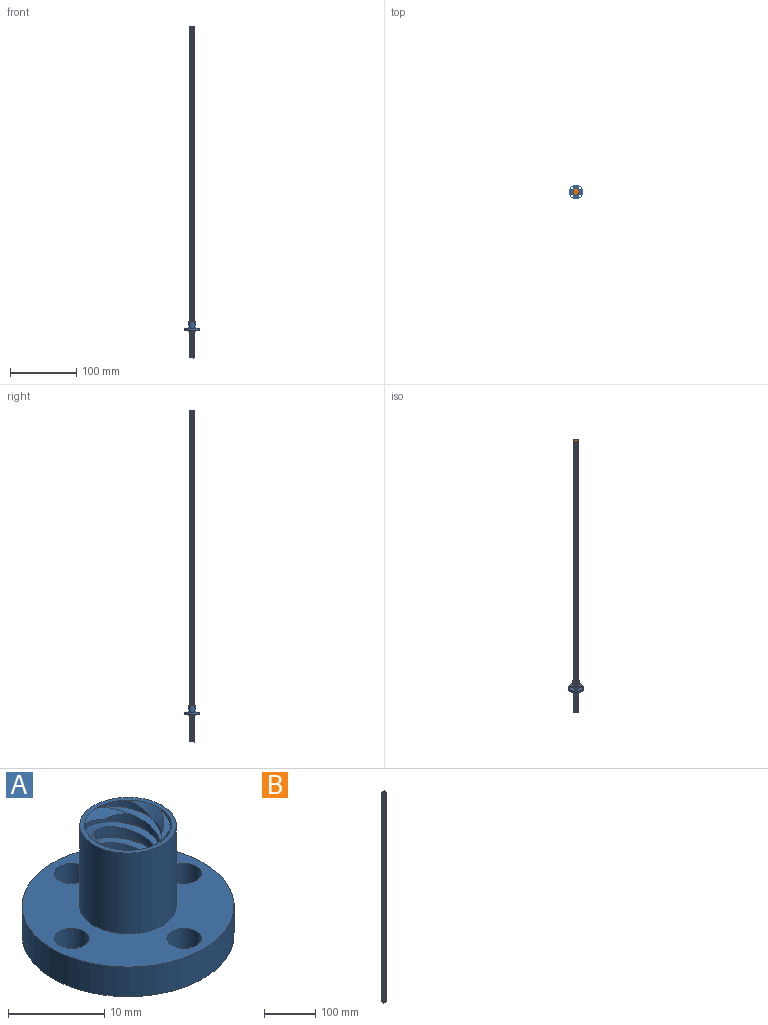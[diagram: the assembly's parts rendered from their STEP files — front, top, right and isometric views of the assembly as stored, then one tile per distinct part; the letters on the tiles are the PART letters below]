
ASSEMBLY  parts=2 mates=1
PART A: 29 faces, bbox 22x22x16 mm
  f0: cylinder r=3.5mm len=13.7mm, axis (0,0,-1), area 54.8mm2, adj f1,f26,f27,f28
  f1: cone r=4.5mm half-angle=45deg, axis (0,0,-1), area 17.8mm2, adj f0,f2,f3,f4,f5,f6,f17,f18
  f2: cylinder r=4.5mm len=15.7mm, axis (0,0,1), area 55.5mm2, adj f1,f3,f26,f27
  f3: bspline ~16x9mm, area 48.6mm2, adj f1,f2,f4,f27
  f4: cylinder r=3.5mm len=13.7mm, axis (0,0,-1), area 54.9mm2, adj f1,f3,f5,f27
  f5: bspline ~16x9mm, area 48.6mm2, adj f1,f4,f17,f27
  f6: plane 10.03x10.03mm, normal (0,0,-1), area 15.4mm2, adj f1,f7
  f7: cylinder r=5.02mm len=10.03mm, axis (0,0,1), area 53.6mm2, adj f6,f8
  f8: plane 22x22mm, normal (0,0,-1), area 260.4mm2, adj f7,f9,f13,f14,f15,f16
  f9: cylinder r=11mm len=22mm, axis (0,0,-1), area 259.2mm2, adj f8,f10
  f10: plane 22x22mm, normal (0,0,1), area 260.4mm2, adj f9,f11,f13,f14,f15,f16
  f11: cylinder r=5.02mm len=10.25mm, axis (0,0,-1), area 323mm2, adj f10,f12
  f12: plane 10.03x10.03mm, normal (0,0,1), area 15.4mm2, adj f11,f27
  f13: cylinder r=1.8mm len=3.75mm, axis (0,0,-1), area 42.4mm2, adj f8,f10
  f14: cylinder r=1.8mm len=3.75mm, axis (0,0,-1), area 42.4mm2, adj f8,f10
  f15: cylinder r=1.8mm len=3.75mm, axis (0,0,-1), area 42.4mm2, adj f8,f10
  f16: cylinder r=1.8mm len=3.75mm, axis (0,0,-1), area 42.4mm2, adj f8,f10
  f17: cylinder r=4.5mm len=15.7mm, axis (0,0,1), area 55.5mm2, adj f1,f5,f18,f27
  f18: bspline ~16x9mm, area 48.6mm2, adj f1,f17,f19,f27
  f19: cylinder r=3.5mm len=13.7mm, axis (0,0,-1), area 35.9mm2, adj f1,f18,f20,f27
  f20: bspline ~16x9mm, area 48.6mm2, adj f1,f19,f21,f27
  f21: cylinder r=4.5mm len=15.7mm, axis (0,0,1), area 55.5mm2, adj f1,f20,f22,f27
  f22: bspline ~16x9mm, area 48.6mm2, adj f1,f21,f23,f27
  f23: cylinder r=3.5mm len=13.7mm, axis (0,0,-1), area 48.1mm2, adj f1,f22,f24,f27
  f24: bspline ~16x9mm, area 48.6mm2, adj f1,f23,f25,f27
  f25: cylinder r=4.5mm len=15.7mm, axis (0,0,1), area 55.5mm2, adj f1,f24,f27,f28
  f26: bspline ~16x9mm, area 48.6mm2, adj f0,f1,f2,f27
  f27: cone r=3.5mm half-angle=45deg, axis (0,0,1), area 17.8mm2, adj f0,f2,f3,f4,f5,f12,f17,f18
  f28: bspline ~16x9mm, area 48.6mm2, adj f0,f1,f25,f27
PART B: 30 faces, bbox 8x8x501 mm
  f0: cylinder r=4mm len=499mm, axis (0,0,-1), area -3136.1mm2, adj f5,f7,f13,f25,f28
  f1: cylinder r=4mm len=499mm, axis (0,0,-1), area -3118.7mm2, adj f5,f6,f12,f14,f23
  f2: cylinder r=4mm len=499mm, axis (0,0,-1), area -3136.1mm2, adj f4,f11,f17,f20,f24
  f3: plane 7x7mm, normal (0,0,1), area 33.4mm2, adj f6,f7,f8,f11,f13,f14,f15,f17
  f4: cone r=4mm half-angle=45deg, axis (0,0,1), area 7.3mm2, adj f2,f9,f10,f16,f17,f20,f29
  f5: cone r=4mm half-angle=45deg, axis (0,0,1), area 7.3mm2, adj f0,f1,f9,f12,f13,f23,f25
  f6: cone r=3.5mm half-angle=45deg, axis (0,0,-1), area 2.1mm2, adj f1,f3,f14,f22,f23
  f7: cone r=3.5mm half-angle=45deg, axis (0,0,-1), area 2.1mm2, adj f0,f3,f13,f28
  f8: cone r=3.5mm half-angle=45deg, axis (0,0,-1), area 2.1mm2, adj f3,f10,f19,f27,f29
  f9: plane 7x7mm, normal (0,0,-1), area 38.5mm2, adj f4,f5,f20,f21,f23,f25,f26,f29
  f10: cylinder r=4mm len=499mm, axis (0,0,-1), area -3118.7mm2, adj f4,f8,f16,f19,f29
  f11: cone r=3.5mm half-angle=45deg, axis (0,0,-1), area 2.1mm2, adj f2,f3,f17,f24
  f12: plane 1x1mm, normal (-1,0,0), area 0.9mm2, adj f1,f5,f13,f14,f15
  f13: bspline ~500x8mm, area 1456.8mm2, adj f0,f3,f5,f7,f12,f15
  f14: bspline ~499x8mm, area 1463.5mm2, adj f1,f3,f6,f12,f15
  f15: cylinder r=3mm len=499.99mm, axis (0,0,-1), area 2179.1mm2, adj f3,f12,f13,f14
  f16: plane 1x1mm, normal (1,0,0), area 0.9mm2, adj f4,f10,f17,f18,f19
  f17: bspline ~500x8mm, area 1464.5mm2, adj f2,f3,f4,f11,f16,f18
  f18: cylinder r=3mm len=499.99mm, axis (0,0,-1), area 2179.1mm2, adj f3,f16,f17,f19
  f19: bspline ~499x8mm, area 1459.3mm2, adj f3,f8,f10,f16,f18
  f20: plane 1.02x1.01mm, normal (0,1,0), area 0.9mm2, adj f2,f4,f9,f21,f24
  f21: cylinder r=3.01mm len=500mm, axis (0,0,-1), area 1828.1mm2, adj f3,f9,f20,f22,f23,f24
  f22: plane 0.49x0mm, normal (0,1,0), area 0mm2, adj f3,f6,f21,f23
  f23: bspline ~500x8.02mm, area 1443.2mm2, adj f1,f5,f6,f9,f21,f22
  f24: bspline ~500x8.02mm, area 1458.8mm2, adj f2,f3,f11,f20,f21
  f25: plane 1.02x1.01mm, normal (0,-1,0), area 0.9mm2, adj f0,f5,f9,f26,f28
  f26: cylinder r=3.01mm len=500mm, axis (0,0,-1), area 1828.1mm2, adj f3,f9,f25,f27,f28,f29
  f27: plane 0.49x0mm, normal (0,-1,0), area 0mm2, adj f3,f8,f26,f29
  f28: bspline ~500x8.02mm, area 1454.6mm2, adj f0,f3,f7,f25,f26
  f29: bspline ~500x8.02mm, area 1450.8mm2, adj f4,f8,f9,f10,f26,f27
PLACE A rot(axis=(0,0,-1),135.2deg) t=(13.54,14.24,41.08)mm
PLACE B rot(axis=(0,0,-1),7.9deg) t=(-0.65,0.14,-0.1)mm
MATE cylindrical A.f0 <-> B.f0  axis (0,0,-1) through (-0.65,0.14,41.08)mm
